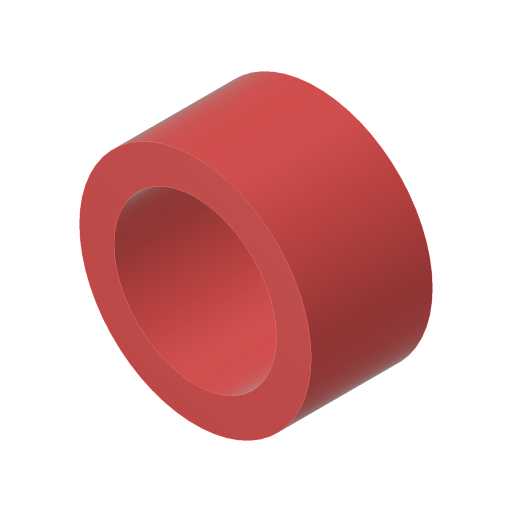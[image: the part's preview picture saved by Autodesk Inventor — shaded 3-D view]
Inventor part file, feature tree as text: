
AUTODESK INVENTOR PART (.ipt)
format: ipt  version: 2023.4 (Build 274418000, 418)  size: 117,248 bytes
history: native  units: in
note: dims shown in document units (in); Inventor stores cm internally (conversion verified against a paired STEP export)
features: extrude x1, sketch x1
ambient origin geometry x8: Origin, YZ Plane, XZ Plane, XY Plane, X Axis, Y Axis, Z Axis, Center Point
bodies: Solid1 (feature_tree)
feature tree (2):
  extrude  "Extrusion1"  Depth=0.437in
  sketch  "Sketch1"  dims[d0=0.585in d1=0.125in d2=0.437in d3=0.0in]
